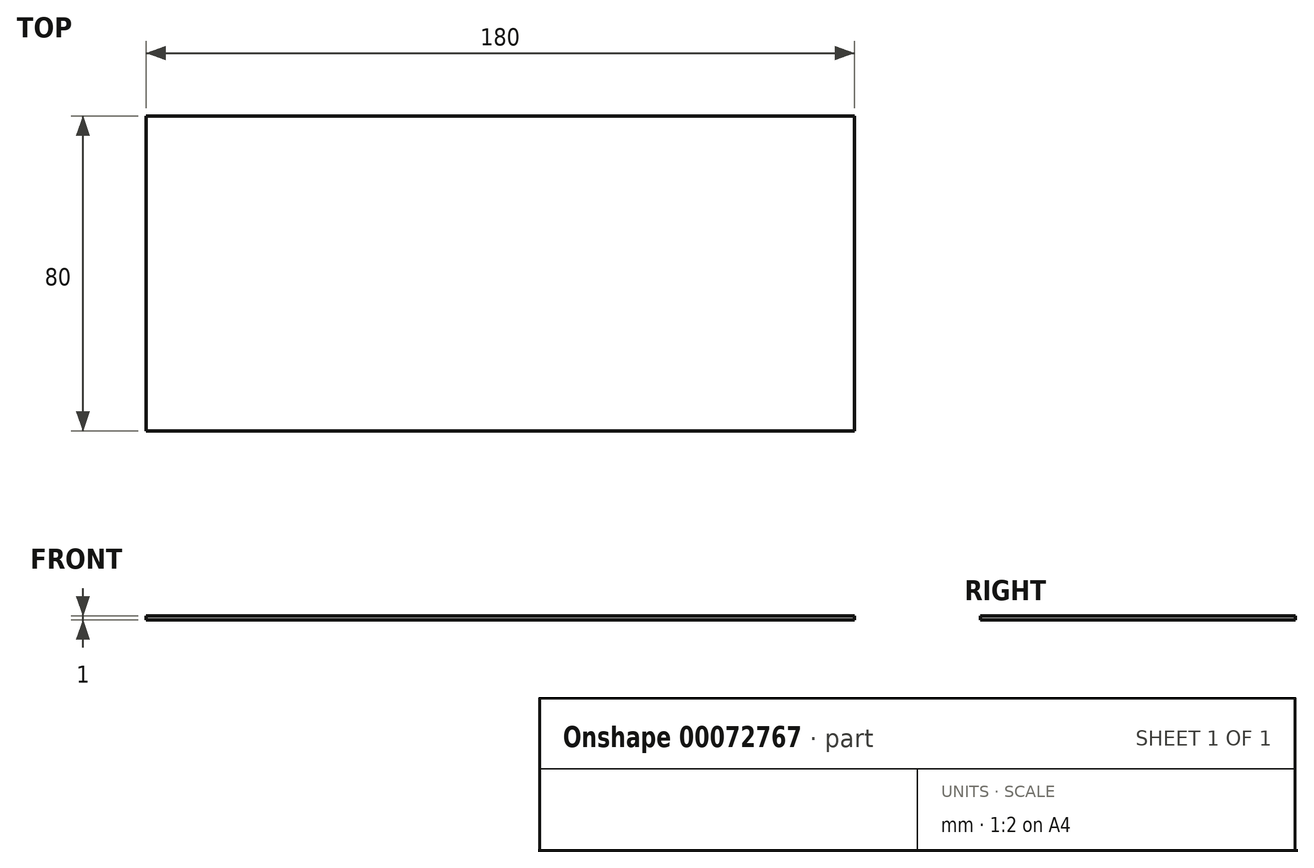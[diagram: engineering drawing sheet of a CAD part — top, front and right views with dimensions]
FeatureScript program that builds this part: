
annotation { "Feature Type Name" : "Feature", "Feature Type Description" : "" }
export const myFeature = defineFeature(function(context is Context, id is Id, definition is map)
    precondition{}
    {
        {
            var Q0;
            Q0=qCreatedBy(makeId("Top.planeOp"),FACE);
            var sketch = newSketch(context, id + "F0", { "sketchPlane" : qUnion([Q0])});
            skLineSegment(sketch, "E0.bottom", {"start": v(-75.92, 46.73) * mm, "end": v(104.08, 46.73) * mm});
            skLineSegment(sketch, "E0.top", {"start": v(-75.92, -33.27) * mm, "end": v(104.08, -33.27) * mm});
            skLineSegment(sketch, "E0.left", {"start": v(-75.92, 46.73) * mm, "end": v(-75.92, -33.27) * mm});
            skLineSegment(sketch, "E0.right", {"start": v(104.08, 46.73) * mm, "end": v(104.08, -33.27) * mm});
            skSolve(sketch);
        }
        {
            var Q0;
            Q0=makeQuery(id+"F0.imprint","IMPRINT",FACE,{"disambiguationData":[TD([[makeQuery(id+"F0.imprint","IMPRINT",EDGE,{"derivedFrom":sQuery(id+"F0.wireOp",EDGE,"E0.bottom")}),-1.0]])]});
            extrude(context, id + "F1", {"entities" : qUnion([Q0]), "depth" : 1 * mm});
        }
    });
